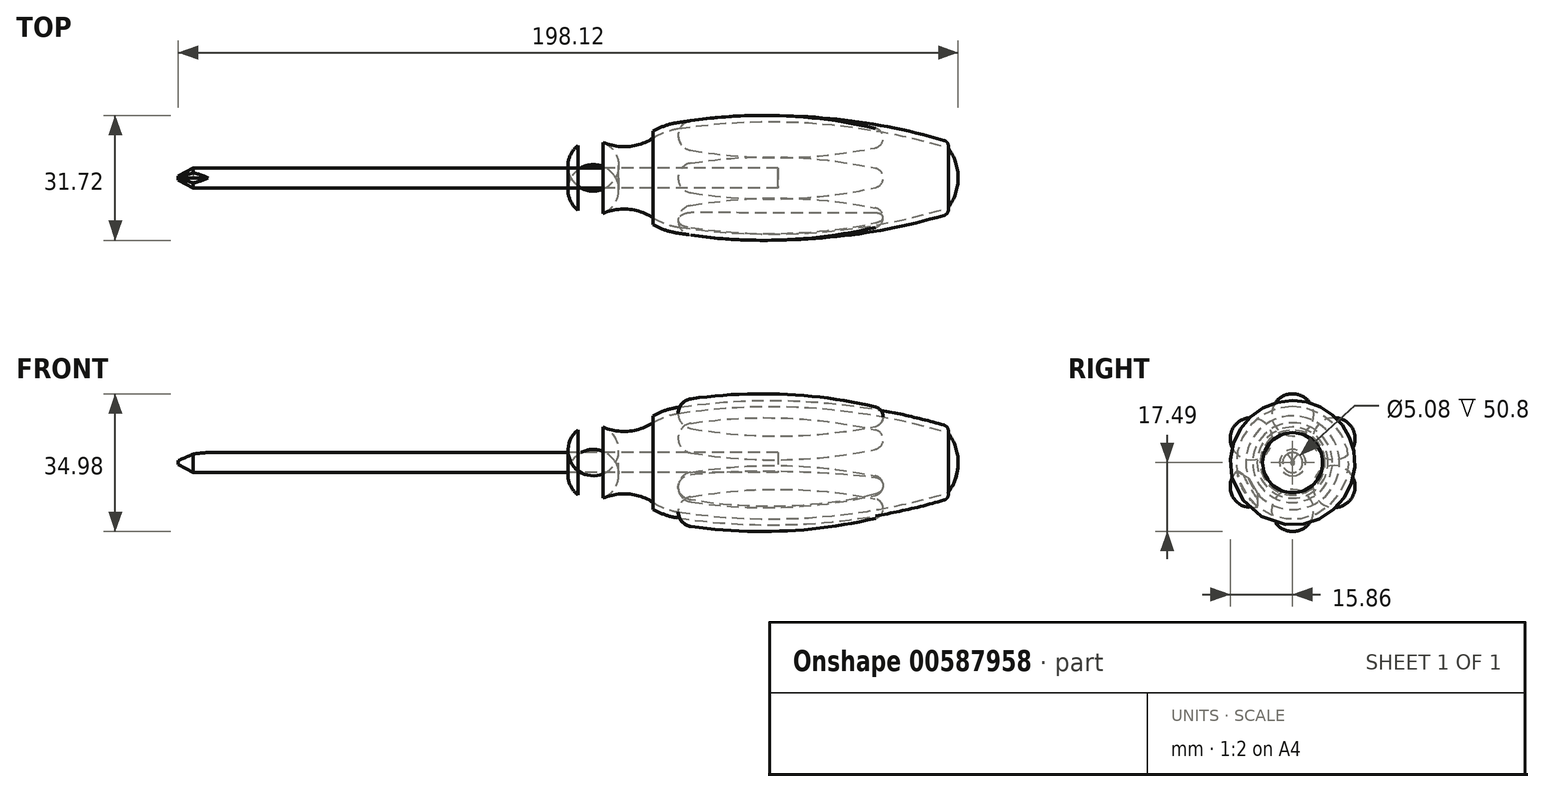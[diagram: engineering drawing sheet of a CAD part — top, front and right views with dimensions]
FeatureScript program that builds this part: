
annotation { "Feature Type Name" : "Feature", "Feature Type Description" : "" }
export const myFeature = defineFeature(function(context is Context, id is Id, definition is map)
    precondition{}
    {
        {
            var Q0;
            Q0=qCreatedBy(makeId("Front.planeOp"),FACE);
            var sketch = newSketch(context, id + "F0", { "sketchPlane" : qUnion([Q0])});
            skLineSegment(sketch, "E0", {"start": v(-101.6, 0) * mm, "end": v(96.52, 0) * mm});
            skLineSegment(sketch, "E1", {"start": v(96.52, 0) * mm, "end": v(117.55, 0) * mm, "construction": true});
            skLineSegment(sketch, "E2", {"start": v(50.8, 2.54) * mm, "end": v(-97.8, 2.54) * mm});
            skLineSegment(sketch, "E3", {"start": v(-101.6, 0.5) * mm, "end": v(-101.6, 0) * mm});
            skLineSegment(sketch, "E4", {"start": v(0, 2.54) * mm, "end": v(0, 8.25) * mm});
            skArc(sketch, "E5", {"start": v(6.35, 9.02) * mm, "mid": v(3.07, 9.48) * mm, "end": v(0, 8.25) * mm});
            skArc(sketch, "E6", {"start": v(6.35, 9.02) * mm, "mid": v(12.84, 7.99) * mm, "end": v(19.05, 10.11) * mm});
            skArc(sketch, "E7", {"start": v(25.4, 12.52) * mm, "mid": v(22.1, 11.65) * mm, "end": v(19.05, 10.11) * mm});
            skArc(sketch, "E8", {"start": v(93.98, 7.62) * mm, "mid": v(59.96, 13.9) * mm, "end": v(25.4, 12.52) * mm});
            skArc(sketch, "E9", {"start": v(96.52, 0) * mm, "mid": v(95.87, 4.02) * mm, "end": v(93.98, 7.62) * mm});
            skArc(sketch, "E10.0", {"start": v(25.17, 14.02) * mm, "mid": v(22.01, 13.24) * mm, "end": v(19.05, 11.9) * mm});
            skArc(sketch, "E10.1", {"start": v(92.95, 9.52) * mm, "mid": v(59.3, 15.46) * mm, "end": v(25.17, 14.02) * mm});
            skLineSegment(sketch, "E11", {"start": v(19.05, 11.9) * mm, "end": v(19.05, 10.11) * mm});
            skArc(sketch, "E12", {"start": v(93.98, 7.62) * mm, "mid": v(93.86, 8.78) * mm, "end": v(92.95, 9.52) * mm});
            skPoint(sketch, "E13.orphan", {"position": v(0, 0) * mm});
            skLineSegment(sketch, "E14", {"start": v(50.8, 2.54) * mm, "end": v(50.8, 0) * mm});
            skLineSegment(sketch, "E15", {"start": v(-101.6, 0.5) * mm, "end": v(-97.8, 2.54) * mm});
            skPoint(sketch, "E16.orphan", {"position": v(-101.6, 2.54) * mm});
            skSolve(sketch);
        }
        {
            var Q0;
            Q0=qCreatedBy(makeId("Front.planeOp"),FACE);
            var sketch = newSketch(context, id + "F1", { "sketchPlane" : qUnion([Q0])});
            skLineSegment(sketch, "E17", {"start": v(25.4, 12.52) * mm, "end": v(77.47, 11.64) * mm});
            skArc(sketch, "E18", {"start": v(28.67, 16.22) * mm, "mid": v(26.35, 14.97) * mm, "end": v(25.4, 12.52) * mm});
            skArc(sketch, "E19", {"start": v(77.47, 11.64) * mm, "mid": v(76.93, 13.25) * mm, "end": v(75.5, 14.16) * mm});
            skArc(sketch, "E20", {"start": v(75.5, 14.16) * mm, "mid": v(52.19, 17.37) * mm, "end": v(28.67, 16.22) * mm});
            skSolve(sketch);
        }
        {
            var Q0;
            Q0=qCreatedBy(makeId("Front.planeOp"),FACE);
            var sketch = newSketch(context, id + "F2", { "sketchPlane" : qUnion([Q0])});
            skLineSegment(sketch, "E21", {"start": v(-101.6, 0.5) * mm, "end": v(-93.98, 2.54) * mm});
            skSolve(sketch);
        }
        {
            var Q0;
            Q0=sQuery(id+"F2.wireOp",VERTEX,"E21.start");
            var Q1;
            Q1=sQuery(id+"F2.wireOp",EDGE,"E21");
            cPlane(context, id + "F3", {"entities" : qUnion([Q0, Q1]), "cplaneType" : CPlaneType.LINE_POINT, "offset" : 25.4 * mm, "width" : 152.4 * mm, "height" : 152.4 * mm});
        }
        {
            var Q0;
            Q0=qCreatedBy(id+"F3.planeOp",FACE);
            var sketch = newSketch(context, id + "F4", { "sketchPlane" : qUnion([Q0])});
            skLineSegment(sketch, "E22", {"start": v(5.08, 29.2) * mm, "end": v(0, 26.67) * mm});
            skLineSegment(sketch, "E23", {"start": v(0, 26.67) * mm, "end": v(-5.08, 29.2) * mm});
            skLineSegment(sketch, "E24", {"start": v(-5.08, 29.2) * mm, "end": v(5.08, 29.2) * mm});
            skLineSegment(sketch, "E25", {"start": v(0, 29.2) * mm, "end": v(0, 26.67) * mm, "construction": true});
            skSolve(sketch);
        }
        {
            var Q0;
            {var subQ0=sQuery(id+"F0.wireOp",EDGE,"E3");Q0=makeQuery(id+"F0.imprint","IMPRINT",FACE,{"disambiguationData":[TD([[makeQuery(id+"F0.imprint","IMPRINT",EDGE,{"derivedFrom":subQ0}),1.0]])]});}
            var Q1;
            Q1=sQuery(id+"F0.wireOp",EDGE,"E0");
            revolve(context, id + "F5", {"entities" : qUnion([Q0]), "axis" : qUnion([Q1]), "revolveType" : RevolveType.FULL});
        }
        {
            var Q0;
            {var subQ0=sQuery(id+"F0.wireOp",EDGE,"E4");Q0=makeQuery(id+"F0.imprint","IMPRINT",FACE,{"disambiguationData":[TD([[makeQuery(id+"F0.imprint","IMPRINT",EDGE,{"derivedFrom":subQ0}),-1.0]])]});}
            var Q1;
            Q1=sQuery(id+"F0.wireOp",EDGE,"E0");
            revolve(context, id + "F6", {"entities" : qUnion([Q0]), "axis" : qUnion([Q1]), "revolveType" : RevolveType.FULL});
        }
        {
            var Q0;
            Q0=makeQuery(id+"F0.imprint","IMPRINT",FACE,{"disambiguationData":[TD([[makeQuery(id+"F0.imprint","IMPRINT",EDGE,{"derivedFrom":sQuery(id+"F0.wireOp",EDGE,"E7")}),-1.0]])]});
            var Q1;
            Q1=sQuery(id+"F0.wireOp",EDGE,"E0");
            revolve(context, id + "F7", {"entities" : qUnion([Q0]), "axis" : qUnion([Q1]), "revolveType" : RevolveType.FULL});
        }
        {
            var Q0;
            Q0=makeQuery(id+"F1.imprint","IMPRINT",FACE,{"disambiguationData":[TD([[makeQuery(id+"F1.imprint","IMPRINT",EDGE,{"derivedFrom":sQuery(id+"F1.wireOp",EDGE,"E17")}),1.0]])]});
            var Q1;
            Q1=sQuery(id+"F1.wireOp",EDGE,"E17");
            revolve(context, id + "F8", {"entities" : qUnion([Q0]), "axis" : qUnion([Q1]), "revolveType" : RevolveType.FULL});
        }
        {
            var Q0;
            Q0=makeQuery(id+"F8.opRevolve","SWEPT_BODY",BODY,{"disambiguationData":[OSD([sQuery(id+"F1.wireOp",EDGE,"E17"),sQuery(id+"F1.wireOp",EDGE,"E18"),sQuery(id+"F1.wireOp",EDGE,"E19"),sQuery(id+"F1.wireOp",EDGE,"E20")])]});
            var Q1;
            Q1=makeQuery(id+"F7.opRevolve","SWEPT_FACE",FACE,{"disambiguationData":[OSD([sQuery(id+"F0.wireOp",EDGE,"E10.1")])]});
            circularPattern(context, id + "F9", {"entities" : qUnion([Q0]), "axis" : qUnion([Q1]), "angle" : 360 * degree, "instanceCount" : 6, "equalSpace" : true});
        }
        {
            var Q0;
            Q0=makeQuery(id+"F6.opRevolve","SWEPT_BODY",BODY,{"disambiguationData":[OSD([sQuery(id+"F0.wireOp",EDGE,"E0"),sQuery(id+"F0.wireOp",EDGE,"E2"),sQuery(id+"F0.wireOp",EDGE,"E4"),sQuery(id+"F0.wireOp",EDGE,"E5"),sQuery(id+"F0.wireOp",EDGE,"E6"),sQuery(id+"F0.wireOp",EDGE,"E7"),sQuery(id+"F0.wireOp",EDGE,"E8"),sQuery(id+"F0.wireOp",EDGE,"E9"),sQuery(id+"F0.wireOp",EDGE,"E14")])]});
            var Q1;
            Q1=makeQuery(id+"F9.opPattern","COPY",BODY,{"derivedFrom":makeQuery(id+"F8.opRevolve","SWEPT_BODY",BODY,{"disambiguationData":[OSD([sQuery(id+"F1.wireOp",EDGE,"E17"),sQuery(id+"F1.wireOp",EDGE,"E18"),sQuery(id+"F1.wireOp",EDGE,"E19"),sQuery(id+"F1.wireOp",EDGE,"E20")])]}),"instanceName":"4"});
            booleanBodies(context, id + "F10", {"operationType" : BooleanOperationType.SUBTRACTION, "tools" : qUnion([Q0]), "targets" : qUnion([Q1]), "keepTools" : true});
        }
        {
            var Q0;
            Q0=makeQuery(id+"F4.imprint","IMPRINT",FACE,{"disambiguationData":[TD([[makeQuery(id+"F4.imprint","IMPRINT",EDGE,{"derivedFrom":sQuery(id+"F4.wireOp",EDGE,"E22")}),-1.0]])]});
            var Q1;
            Q1=sQuery(id+"F2.wireOp",EDGE,"E21");
            sweep(context, id + "F11", {"operationType" : NewBodyOperationType.REMOVE, "profiles" : qUnion([Q0]), "path" : qUnion([Q1])});
        }
    });
